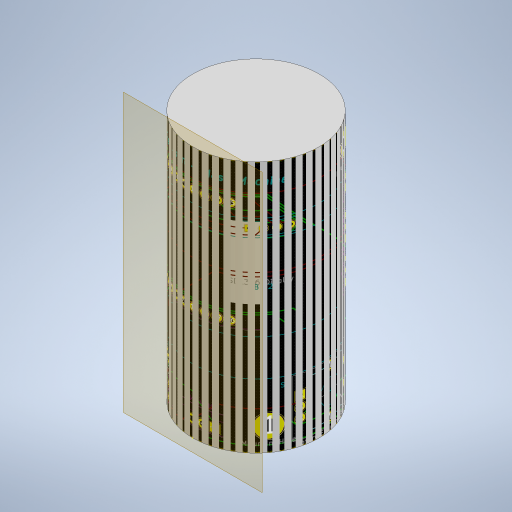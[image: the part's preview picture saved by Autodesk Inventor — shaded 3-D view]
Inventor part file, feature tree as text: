
AUTODESK INVENTOR PART (.ipt)
format: ipt  version: 2024 (Build 280153000, 153)  size: 627,712 bytes
history: native  units: mm
features: sketch x3, other x2, extrude x1, plane x1
ambient origin geometry x8: Origin, YZ Plane, XZ Plane, XY Plane, X Axis, Y Axis, Z Axis, Center Point
bodies: Solid1 (feature_tree)
feature tree (7):
  extrude  "Extrusion1"  Depth=20.0mm TaperAngle=0.0deg
  plane  "Work Plane1"
  other  "Decal1"
  sketch  "Sketch5"
  sketch  "Sketch3"  dims[d7=10.0mm d8=20.0mm d9=0.0mm]
  sketch  "Sketch4"
  other  "Image2"
